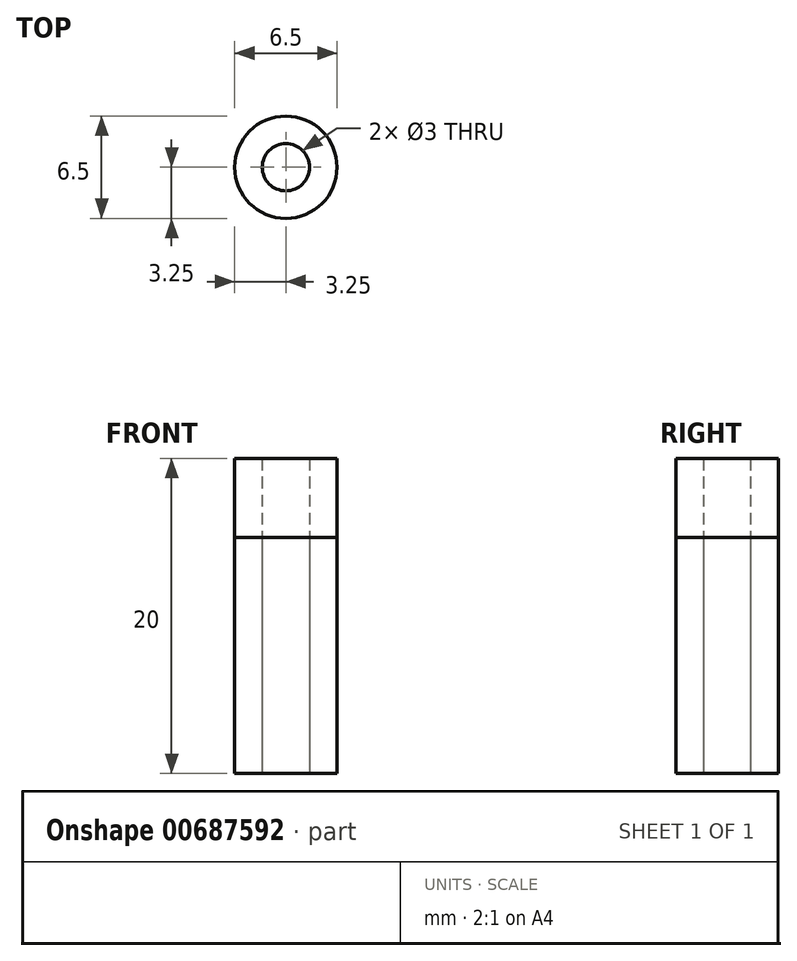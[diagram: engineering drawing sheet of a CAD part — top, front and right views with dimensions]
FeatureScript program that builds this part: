
annotation { "Feature Type Name" : "Feature", "Feature Type Description" : "" }
export const myFeature = defineFeature(function(context is Context, id is Id, definition is map)
    precondition{}
    {
        {
            var Q0;
            Q0=qCreatedBy(makeId("Top.planeOp"),FACE);
            var sketch = newSketch(context, id + "F0", { "sketchPlane" : qUnion([Q0])});
            skCircle(sketch, "E0", {"center": v(0, 0) * mm, "radius": 3.25 * mm});
            skCircle(sketch, "E1", {"center": v(0, 0) * mm, "radius": 1.5 * mm});
            skSolve(sketch);
        }
        {
            var Q0;
            Q0=qSketchRegion(id+"F0",true);
            extrude(context, id + "F1", {"entities" : qUnion([Q0]), "depth" : 15 * mm, "offsetDistance" : 25 * mm});
        }
        {
            var Q0;
            Q0=qSketchRegion(id+"F0",true);
            extrude(context, id + "F2", {"entities" : qUnion([Q0]), "depth" : 20 * mm, "offsetDistance" : 25 * mm});
        }
    });
